# Revit family: VTp752 Угольник 90 с переходом на ВР
name_source: partatom
category: Соединительные детали трубопроводов
revit_build: Autodesk Revit 2015 (Build: 20140606_1530(x64)
units: mm (PartAtom-declared; Revit-internal decimal feet)

## types (6) — shared parameters
Группа модели = VTp.700
Изготовитель = VALTEC S.R.L.
Коэффициент K = 0.5
Метод определения потерь = Коэффициент K
Описание = Угольник 90 с переходом на внутр. резьбу
Таблица коэффициентов K = Angle Valve Threaded

## per-type parameters (varying)
| type | 20х1/2" | 20х3/4" | 25х1/2" | 25х3/4" | 32х1" | 32х3/4" | A | B | C | G | Lrez | d | Глубина вхождения | Код по классификатору |
| 20х1/2" | Да | Нет | Нет | Нет | Нет | Нет | 27 мм | 15 мм | 31 мм | 15 мм | 14 мм | 20 мм | 11 мм | VTp.752.0.02004 |
| 20х3/4" | Нет | Да | Нет | Нет | Нет | Нет | 32 мм | 15 мм | 32 мм | 20 мм | 14 мм | 20 мм | 11 мм | VTp.752.0.02005 |
| 25х1/2" | Нет | Нет | Да | Нет | Нет | Нет | 30 мм | 17 мм | 35 мм | 15 мм | 14 мм | 25 мм | 11 мм | VTp.752.0.02504 |
| 25х3/4" | Нет | Нет | Нет | Да | Нет | Нет | 31 мм | 17 мм | 35 мм | 20 мм | 14 мм | 25 мм | 11 мм | VTp.752.0.02505 |
| 32х3/4" | Нет | Нет | Нет | Нет | Нет | Да | 39 мм | 18 мм | 42 мм | 20 мм | 14 мм | 32 мм | 11 мм | VTp.752.0.03205 |
| 32х1" | Нет | Нет | Нет | Нет | Да | Нет | 39 мм | 18 мм | 44 мм | 25 мм | 18 мм | 32 мм | 14 мм | VTp.752.0.03206 |
